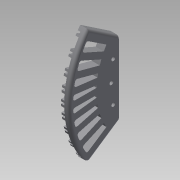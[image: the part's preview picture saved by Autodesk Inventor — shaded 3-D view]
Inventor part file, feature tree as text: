
AUTODESK INVENTOR PART (.ipt)
format: ipt  version: 2015 (Build 190159000, 159)  size: 543,232 bytes
history: native  units: in
note: dims shown in document units (in); Inventor stores cm internally (conversion verified against a paired STEP export)
features: extrude x4, plane x3, sketch x3, fillet x1
ambient origin geometry x8: Origin, YZ Plane, XZ Plane, XY Plane, X Axis, Y Axis, Z Axis, Center Point
bodies: Solid1 (feature_tree)
feature tree (11):
  plane  "Work Plane1"
  extrude  "Extrusion1"  Depth=0.12in
  sketch  "Sketch3"  dims[d0=1.9685in d1=0.12in]
  plane  "Work Plane4"
  extrude  "Extrusion3"  Depth=3.3465in
  extrude  "Extrusion6"  Depth=0.0787in
  plane  "Work Plane5"
  fillet  "Fillet6"  Radius=2.9921in
  extrude  "Extrusion8"  Depth=0.0787in
  sketch  "Sketch6"  dims[d2=1.2598in d3=3.3465in]
  sketch  "Sketch9"  dims[d4=1.2598in d5=3.0709in d6=2.9921in d7=2.3622in d8=45.0deg d10=0.1614in d11=0.0in d12=2.9567in d14=2.6614in d15=0.0906in d16=3.0472in d17=0.268in d18=0.268in d25=0.0669in d26=0.0669in d28=0.1969in d30=3.1496in d31=3.0709in d32=3.0709in d37=0.7874in d39=0.0481in d41=0.0984in d42=0.0in d68=3.1496in d70=0.4329in d82=0.0984in d83=0.0in d84=2.0472in d86=2.2047in d87=0.0394in d89=-1.1811in d94=0.0787in d95=1.7323in d96=0.2992in d97=0.0945in d98=0.0945in d99=0.7874in d101=0.055in d106=2.0472in d107=2.126in d109=0.7874in d111=0.0618in d113=0.7874in d115=0.0653in d117=2.9567in d118=0.2336in d119=0.1969in d120=2.9528in d121=0.0591in d122=2.9528in d123=2.9528in d124=2.9528in d125=0.0591in d129=0.0787in d130=0.2067in d131=0.0591in d132=1.8898in d133=0.0591in d134=0.0984in d135=0.0787in d137=1.4585in d138=0.2336in d139=0.0039in d140=0.0039in d141=1.2598in d142=0.0039in d143=0.0in]
